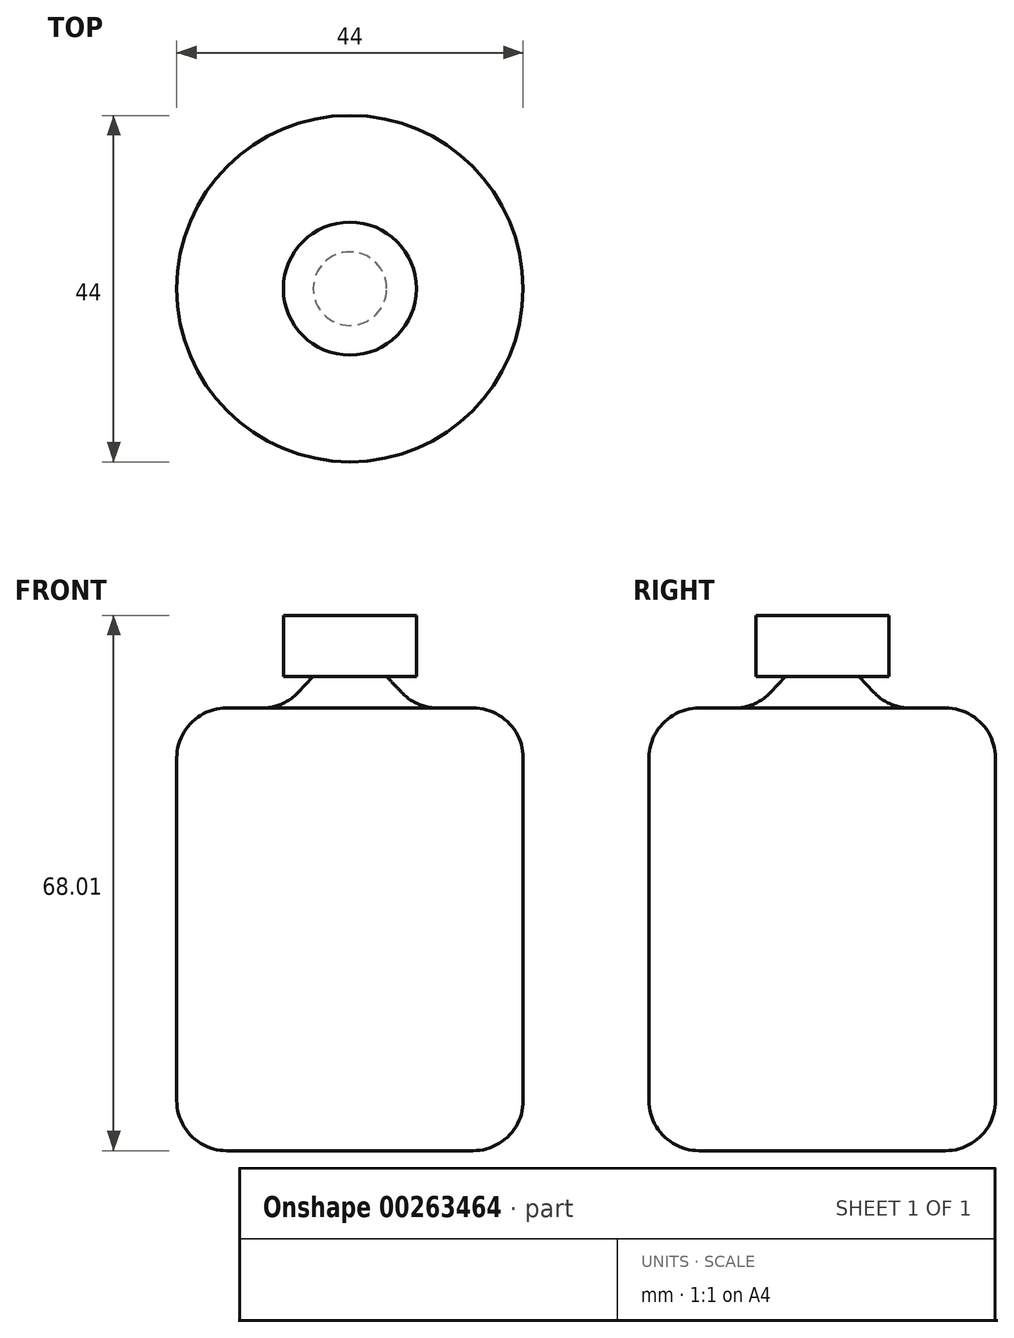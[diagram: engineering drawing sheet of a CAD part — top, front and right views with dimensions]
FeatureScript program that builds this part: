
annotation { "Feature Type Name" : "Feature", "Feature Type Description" : "" }
export const myFeature = defineFeature(function(context is Context, id is Id, definition is map)
    precondition{}
    {
        {
            var Q0;
            Q0=qCreatedBy(makeId("Front.planeOp"),FACE);
            var sketch = newSketch(context, id + "F0", { "sketchPlane" : qUnion([Q0])});
            skLineSegment(sketch, "E0", {"start": v(0, 0) * mm, "end": v(-15.65, 0) * mm});
            skLineSegment(sketch, "E1", {"start": v(-22, 6.35) * mm, "end": v(-22, 49.88) * mm});
            skLineSegment(sketch, "E2", {"start": v(-15.65, 56.23) * mm, "end": v(-11.18, 56.23) * mm});
            skLineSegment(sketch, "E3", {"start": v(-6.57, 58.22) * mm, "end": v(-4.67, 60.23) * mm});
            skLineSegment(sketch, "E4", {"start": v(-4.67, 60.23) * mm, "end": v(-8.45, 60.23) * mm});
            skLineSegment(sketch, "E5", {"start": v(-8.45, 60.23) * mm, "end": v(-8.45, 68) * mm});
            skLineSegment(sketch, "E6", {"start": v(-8.45, 68) * mm, "end": v(0, 68) * mm});
            skLineSegment(sketch, "E7", {"start": v(0, 68) * mm, "end": v(0, 0) * mm});
            skPoint(sketch, "E8.visualSharp", {"position": v(-8.45, 56.23) * mm});
            skArc(sketch, "E8.filletArc", {"start": v(-11.18, 56.23) * mm, "mid": v(-8.67, 56.75) * mm, "end": v(-6.57, 58.22) * mm});
            skPoint(sketch, "E9.visualSharp", {"position": v(-22, 56.23) * mm});
            skArc(sketch, "E9.filletArc", {"start": v(-15.65, 56.23) * mm, "mid": v(-20.14, 54.37) * mm, "end": v(-22, 49.88) * mm});
            skPoint(sketch, "E10.visualSharp", {"position": v(-22, 0) * mm});
            skArc(sketch, "E10.filletArc", {"start": v(-22, 6.35) * mm, "mid": v(-20.14, 1.86) * mm, "end": v(-15.65, 0) * mm});
            skSolve(sketch);
        }
        {
            var Q0;
            Q0=makeQuery(id+"F0.imprint","IMPRINT",FACE,{"disambiguationData":[TD([[makeQuery(id+"F0.imprint","IMPRINT",EDGE,{"derivedFrom":sQuery(id+"F0.wireOp",EDGE,"E0")}),-1.0]])]});
            var Q1;
            Q1=sQuery(id+"F0.wireOp",EDGE,"E7");
            revolve(context, id + "F1", {"entities" : qUnion([Q0]), "axis" : qUnion([Q1]), "revolveType" : RevolveType.FULL});
        }
    });
